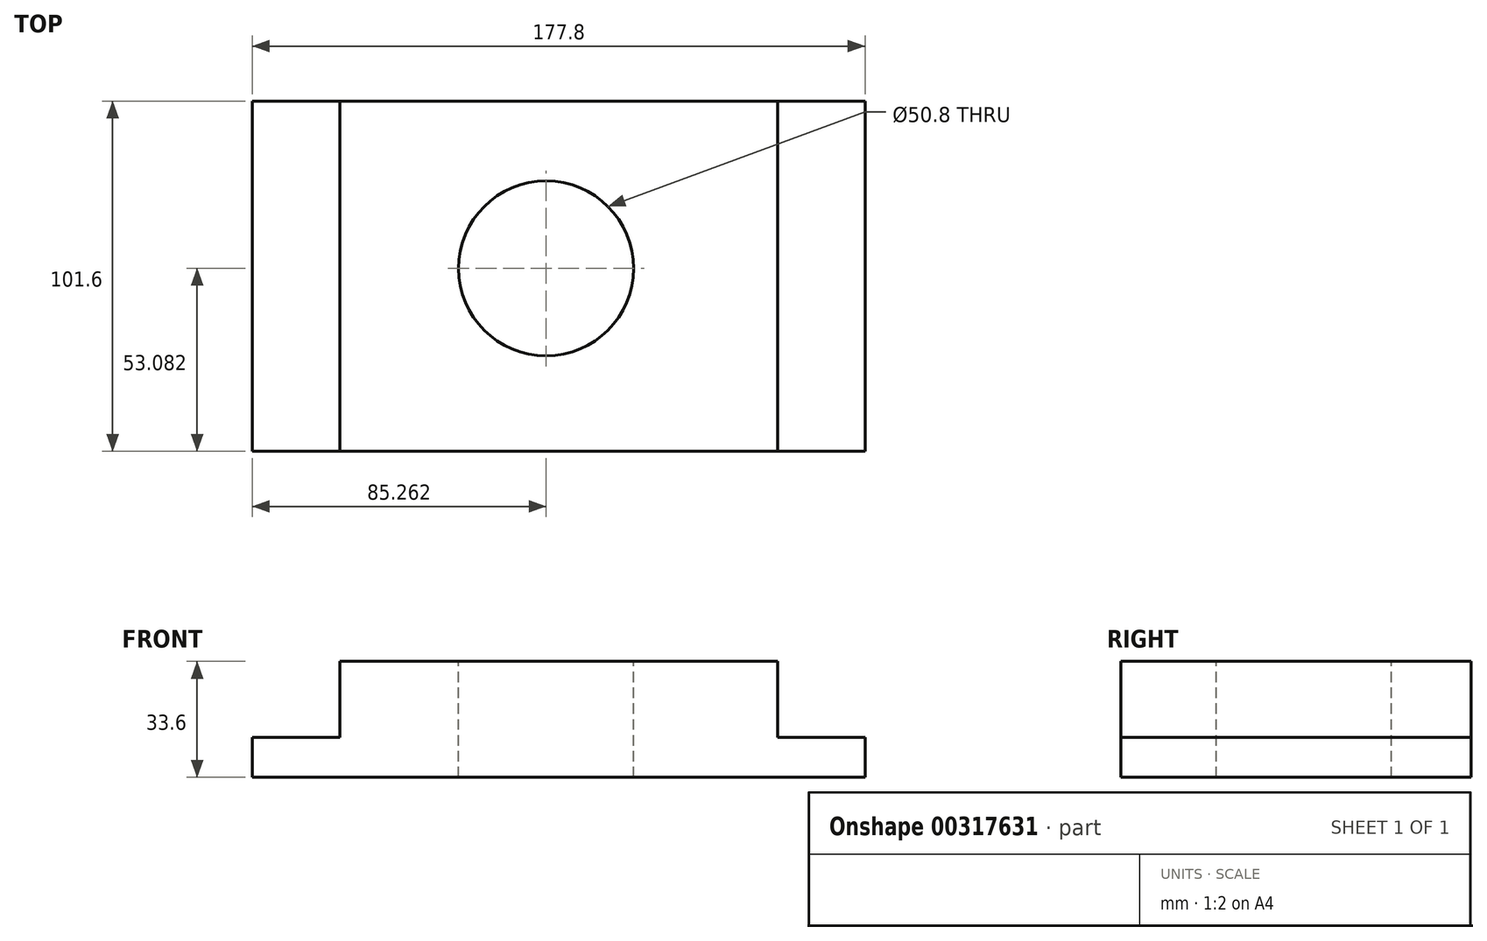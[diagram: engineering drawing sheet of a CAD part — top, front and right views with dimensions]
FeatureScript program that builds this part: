
annotation { "Feature Type Name" : "Feature", "Feature Type Description" : "" }
export const myFeature = defineFeature(function(context is Context, id is Id, definition is map)
    precondition{}
    {
        {
            var Q0;
            Q0=qCreatedBy(makeId("Front.planeOp"),FACE);
            var sketch = newSketch(context, id + "F0", { "sketchPlane" : qUnion([Q0])});
            skLineSegment(sketch, "E0.bottom", {"start": v(0, 0) * mm, "end": v(177.8, 0) * mm});
            skLineSegment(sketch, "E0.top", {"start": v(0, 33.6) * mm, "end": v(177.8, 33.6) * mm});
            skLineSegment(sketch, "E0.left", {"start": v(0, 0) * mm, "end": v(0, 33.6) * mm});
            skLineSegment(sketch, "E0.right", {"start": v(177.8, 0) * mm, "end": v(177.8, 33.6) * mm});
            skSolve(sketch);
        }
        {
            var Q0;
            Q0 = qSketchRegion(id + "F0", true);
            extrude(context, id + "F1", {"entities" : qUnion([Q0]), "depth" : 101.6 * mm});
        }
        {
            var Q0;
            Q0=makeQuery(id+"F1.opExtrude","SWEPT_FACE",FACE,{"disambiguationData":[OSD([sQuery(id+"F0.wireOp",EDGE,"E0.top")])]});
            var sketch = newSketch(context, id + "F2", { "sketchPlane" : qUnion([Q0])});
            skCircle(sketch, "E1", {"center": v(85.26, -48.52) * mm, "radius": 25.4 * mm});
            skSolve(sketch);
        }
        {
            var Q0;
            Q0 = qSketchRegion(id + "F2", true);
            extrude(context, id + "F3", {"entities" : qUnion([Q0]), "operationType" : NewBodyOperationType.REMOVE, "endBound" : BoundingType.THROUGH_ALL, "oppositeDirection" : true, "depth" : 25.4 * mm});
        }
        {
            var Q0;
            Q0=makeQuery(id+"F1.opExtrude","CAP_FACE",FACE,{"disambiguationData":[OSD([sQuery(id+"F0.wireOp",EDGE,"E0.bottom"),sQuery(id+"F0.wireOp",EDGE,"E0.top"),sQuery(id+"F0.wireOp",EDGE,"E0.left"),sQuery(id+"F0.wireOp",EDGE,"E0.right")])],"isStart":false});
            var sketch = newSketch(context, id + "F4", { "sketchPlane" : qUnion([Q0])});
            skLineSegment(sketch, "E2.bottom", {"start": v(177.8, 33.6) * mm, "end": v(159.56, 33.6) * mm});
            skLineSegment(sketch, "E3.bottom", {"start": v(0, 33.6) * mm, "end": v(25.4, 33.6) * mm});
            skLineSegment(sketch, "E3.top", {"start": v(0, 11.6) * mm, "end": v(25.4, 11.6) * mm});
            skLineSegment(sketch, "E3.left", {"start": v(0, 33.6) * mm, "end": v(0, 11.6) * mm});
            skLineSegment(sketch, "E3.right", {"start": v(25.4, 33.6) * mm, "end": v(25.4, 11.6) * mm});
            skLineSegment(sketch, "E4.bottom", {"start": v(177.8, 33.6) * mm, "end": v(152.4, 33.6) * mm});
            skLineSegment(sketch, "E4.top", {"start": v(177.8, 11.6) * mm, "end": v(152.4, 11.6) * mm});
            skLineSegment(sketch, "E4.left", {"start": v(177.8, 33.6) * mm, "end": v(177.8, 11.6) * mm});
            skLineSegment(sketch, "E4.right", {"start": v(152.4, 33.6) * mm, "end": v(152.4, 11.6) * mm});
            skSolve(sketch);
        }
        {
            var Q0;
            Q0 = qSketchRegion(id + "F4", true);
            extrude(context, id + "F5", {"entities" : qUnion([Q0]), "operationType" : NewBodyOperationType.REMOVE, "endBound" : BoundingType.THROUGH_ALL, "oppositeDirection" : true, "depth" : 25.4 * mm});
        }
    });
